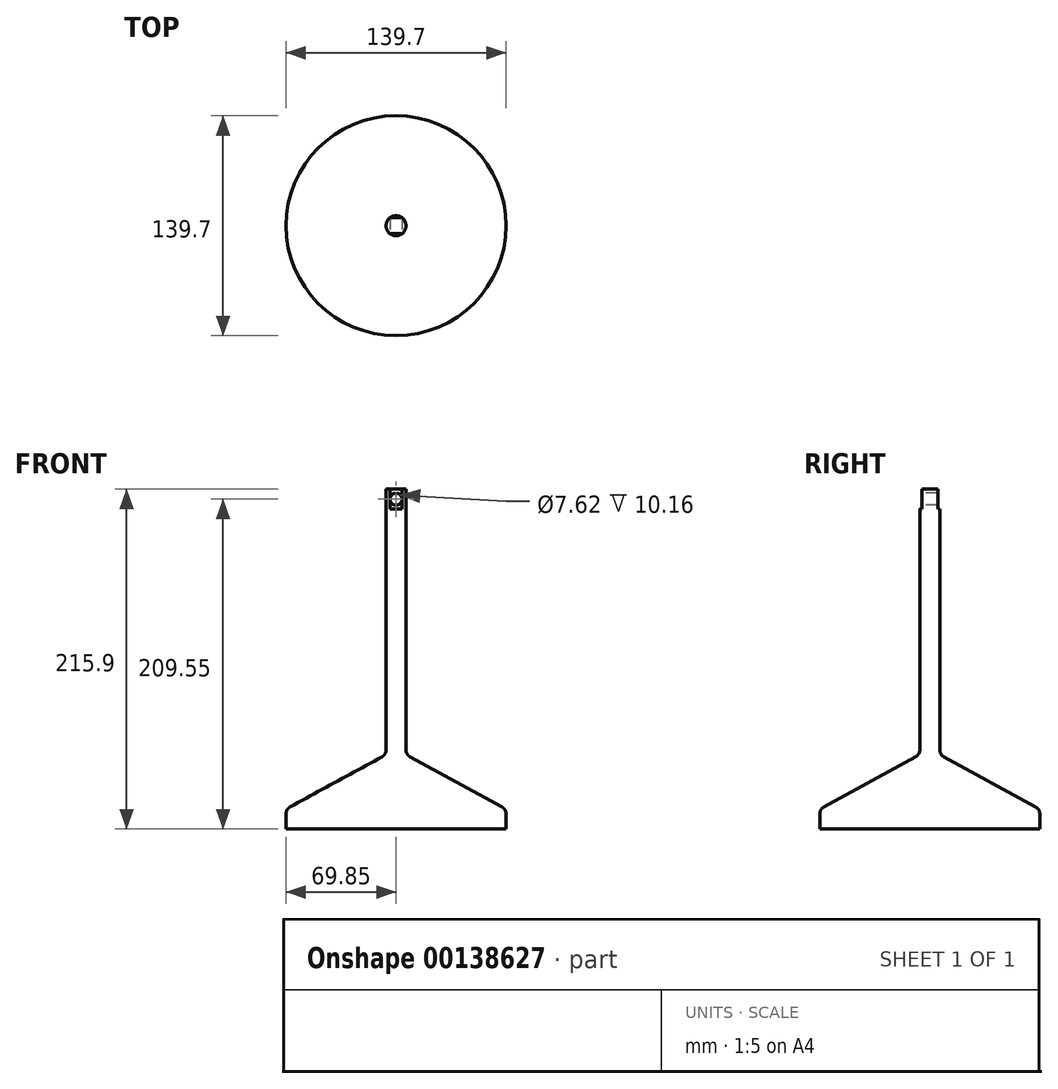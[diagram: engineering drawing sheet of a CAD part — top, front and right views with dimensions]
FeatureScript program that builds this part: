
annotation { "Feature Type Name" : "Feature", "Feature Type Description" : "" }
export const myFeature = defineFeature(function(context is Context, id is Id, definition is map)
    precondition{}
    {
        {
            var Q0;
            Q0=qCreatedBy(makeId("Top.planeOp"),FACE);
            var sketch = newSketch(context, id + "F0", { "sketchPlane" : qUnion([Q0])});
            skCircle(sketch, "E0", {"center": v(0, 0) * mm, "radius": 69.85 * mm});
            skSolve(sketch);
        }
        {
            var Q0;
            Q0 = qSketchRegion(id + "F0", true);
            extrude(context, id + "F1", {"entities" : qUnion([Q0]), "depth" : 12.7 * mm});
        }
        {
            var Q0;
            Q0=qCreatedBy(makeId("Front.planeOp"),FACE);
            var sketch = newSketch(context, id + "F2", { "sketchPlane" : qUnion([Q0])});
            skLineSegment(sketch, "E1", {"start": v(-69.85, 12.7) * mm, "end": v(0, 50.8) * mm});
            skLineSegment(sketch, "E2", {"start": v(0, 50.8) * mm, "end": v(0, 12.7) * mm});
            skLineSegment(sketch, "E3", {"start": v(0, 12.7) * mm, "end": v(-69.85, 12.7) * mm});
            skSolve(sketch);
        }
        {
            var Q0;
            Q0 = qSketchRegion(id + "F2", true);
            var Q1;
            Q1=sQuery(id+"F2.wireOp",EDGE,"E2");
            revolve(context, id + "F3", {"operationType" : NewBodyOperationType.ADD, "entities" : qUnion([Q0]), "axis" : qUnion([Q1]), "revolveType" : RevolveType.FULL});
        }
        {
            var Q0;
            Q0=makeQuery(id+"F3.boolean.opBoolean","MERGE",EDGE,{"derivedFrom":[makeQuery(id+"F1.opExtrude","CAP_EDGE",EDGE,{"disambiguationData":[OSD([sQuery(id+"F0.wireOp",EDGE,"E0")])],"isStart":false}),makeQuery(id+"F3.opRevolve","SWEPT_EDGE",EDGE,{"disambiguationData":[OSD([sQuery(id+"F2.wireOp",EDGE,"E1"),sQuery(id+"F2.wireOp",EDGE,"E3")])]})]});
            fillet(context, id + "F4", {"entities" : qUnion([Q0]), "radius" : 5.08 * mm, "tangentPropagation" : true, "allowEdgeOverflow" : false});
        }
        {
            var Q0;
            Q0=qCreatedBy(makeId("Top.planeOp"),FACE);
            var sketch = newSketch(context, id + "F5", { "sketchPlane" : qUnion([Q0])});
            skCircle(sketch, "E4", {"center": v(0, 0) * mm, "radius": 6.35 * mm});
            skSolve(sketch);
        }
        {
            var Q0;
            Q0 = qSketchRegion(id + "F5", true);
            extrude(context, id + "F6", {"entities" : qUnion([Q0]), "operationType" : NewBodyOperationType.ADD, "depth" : 203.2 * mm});
        }
        {
            var Q0;
            Q0=makeQuery(id+"F6.opExtrude","CAP_FACE",FACE,{"disambiguationData":[OSD([sQuery(id+"F5.wireOp",EDGE,"E4")])],"isStart":false});
            var sketch = newSketch(context, id + "F7", { "sketchPlane" : qUnion([Q0])});
            skLineSegment(sketch, "E5", {"start": v(-3.8, -5.08) * mm, "end": v(3.8, -5.08) * mm});
            skArc(sketch, "E6", {"start": v(3.8, -5.08) * mm, "mid": v(6.35, 0) * mm, "end": v(3.8, 5.08) * mm});
            skArc(sketch, "E7", {"start": v(-3.81, 5.08) * mm, "mid": v(-6.35, 0) * mm, "end": v(-3.8, -5.08) * mm});
            skLineSegment(sketch, "E8", {"start": v(-3.8, 5.08) * mm, "end": v(3.8, 5.08) * mm});
            skSolve(sketch);
        }
        {
            var Q0;
            Q0 = qSketchRegion(id + "F7", true);
            extrude(context, id + "F8", {"entities" : qUnion([Q0]), "operationType" : NewBodyOperationType.ADD, "depth" : 12.7 * mm});
        }
        {
            var Q0;
            Q0=makeQuery(id+"F8.opExtrude","SWEPT_FACE",FACE,{"disambiguationData":[OSD([sQuery(id+"F7.wireOp",EDGE,"E5")])]});
            var sketch = newSketch(context, id + "F9", { "sketchPlane" : qUnion([Q0])});
            skCircle(sketch, "E9", {"center": v(0, 209.55) * mm, "radius": 3.81 * mm});
            skPoint(sketch, "E9.centerSnap0", {"position": v(-3.8, 209.55) * mm});
            skSolve(sketch);
        }
        {
            var Q0;
            Q0 = qSketchRegion(id + "F9", true);
            extrude(context, id + "F10", {"entities" : qUnion([Q0]), "operationType" : NewBodyOperationType.REMOVE, "endBound" : BoundingType.SYMMETRIC, "oppositeDirection" : true, "depth" : 25.4 * mm});
        }
        {
            var Q0;
            Q0=makeQuery(id+"F3.opRevolve","SWEPT_FACE",FACE,{"disambiguationData":[OSD([sQuery(id+"F2.wireOp",EDGE,"E1")])]});
            fillet(context, id + "F11", {"entities" : qUnion([Q0]), "radius" : 5.08 * mm, "tangentPropagation" : true, "allowEdgeOverflow" : false});
        }
    });
